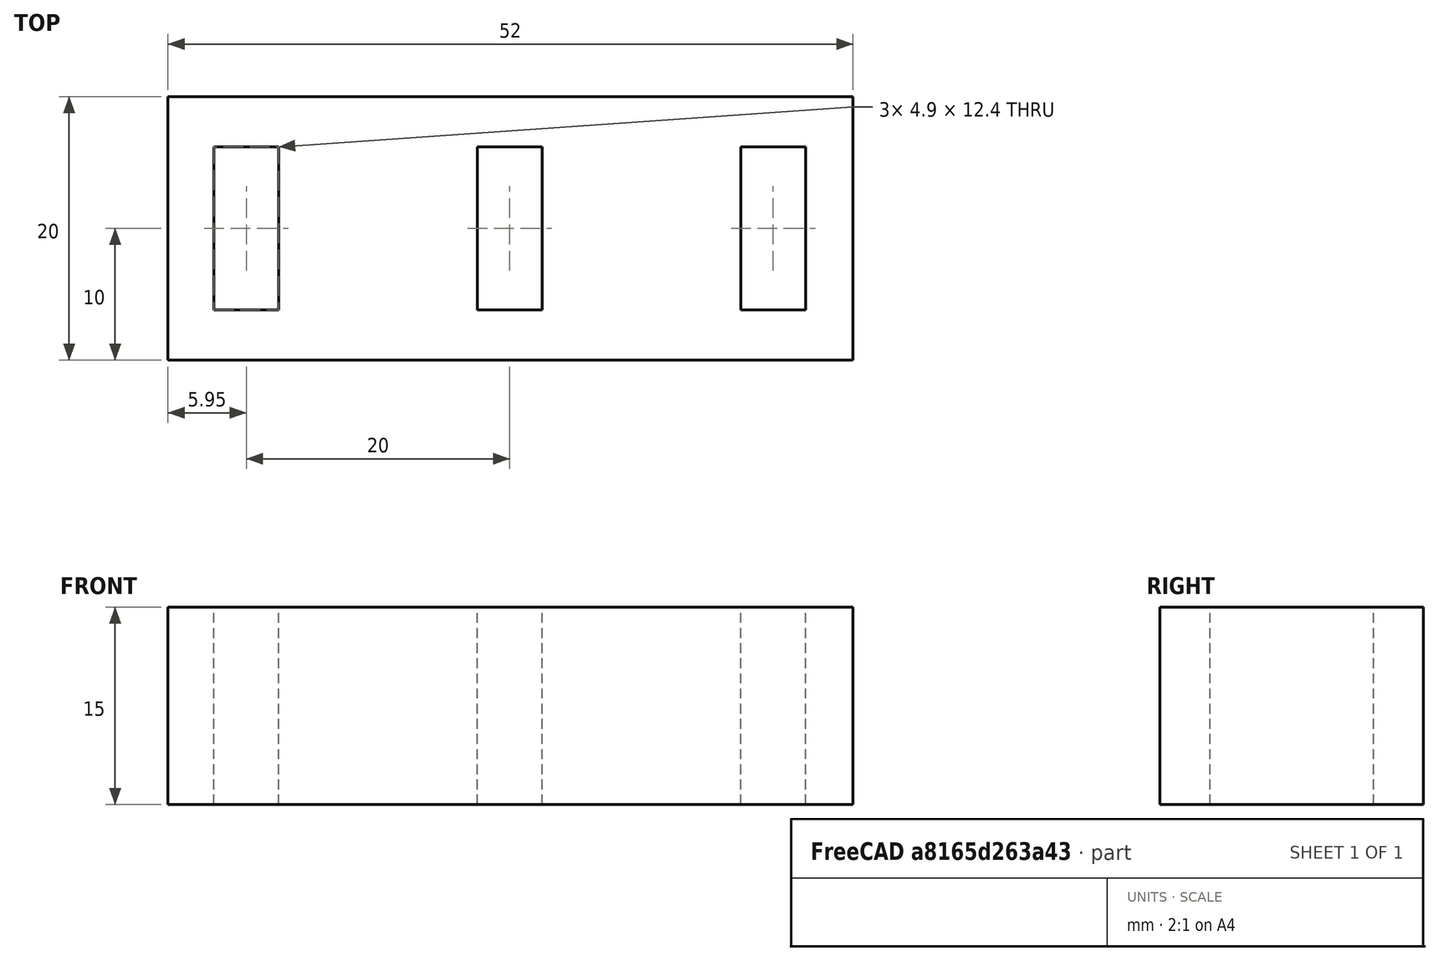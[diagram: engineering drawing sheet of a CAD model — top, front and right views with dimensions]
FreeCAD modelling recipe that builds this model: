
FCSTD DOCUMENT  (FreeCAD 1.0R38806 (Git))
Label: portapendrives
License: All rights reserved
LicenseURL: https://en.wikipedia.org/wiki/All_rights_reserved
objects: App::FeaturePython×8, Part::Box×4, Part::MultiFuse×1, Part::Cut×1
note: 6 computed .brp shape members not serialized (recipe doc carries the construction recipe); baked Part::Feature solids carry a one-line shape summary decoded from their .brp

FEATURE [Part::Box] Box  label="Cube"
  AttacherType = Attacher::AttachEngine3D
  Height = 15
  Length = 52
  Width = 20
FEATURE [Part::Box] Box001  label="Cube001"
  AttacherType = Attacher::AttachEngine3D
  Height = 23
  Length = 4.9
  Placement = pos=(3.5,3.8,-3) rot=(0,0,1;0rad)
  Width = 12.4
FEATURE [Part::Box] Box002  label="Cube002"
  AttacherType = Attacher::AttachEngine3D
  Height = 23
  Length = 4.9
  Placement = pos=(23.5,3.8,-3) rot=(0,0,1;0rad)
  Width = 12.4
FEATURE [Part::Box] Box003  label="Cube003"
  AttacherType = Attacher::AttachEngine3D
  Height = 23
  Length = 4.9
  Placement = pos=(43.5,3.8,-3) rot=(0,0,1;0rad)
  Width = 12.4
FEATURE [Part::MultiFuse] Fusion
  Refine = true
  Shapes = -> [Box003,Box002,Box001]
FEATURE [Part::Cut] Cut
  Base = -> Box
  Refine = true
  Tool = -> Fusion
FEATURE [App::FeaturePython] Dimension  # Draft dimension (typed FeaturePython)
  Diameter = false
  Dimline = (0,16.2,15)
  Direction = (0,0,0)
  Distance = 3.5
  End = (0,16.2,15)
  Normal = (0,0,1)
  Start = (3.5,16.2,15)
FEATURE [App::FeaturePython] Dimension001  # Draft dimension (typed FeaturePython)
  Diameter = false
  Dimline = (52,20.4279,15)
  Direction = (0,0,0)
  Distance = 52
  End = (52,20,15)
  Normal = (0,0,1)
  Start = (0,20,15)
FEATURE [App::FeaturePython] Dimension002  # Draft dimension (typed FeaturePython)
  Diameter = false
  Dimline = (8.4,3.8,15)
  Direction = (0,0,0)
  Distance = 12.4
  End = (8.4,3.8,15)
  Normal = (0,0,1)
  Start = (8.4,16.2,15)
FEATURE [App::FeaturePython] Dimension003  # Draft dimension (typed FeaturePython)
  Diameter = false
  Dimline = (28.4,3.8,15)
  Direction = (0,0,0)
  Distance = 4.9
  End = (28.4,3.8,15)
  Normal = (0,0,1)
  Start = (23.5,3.8,15)
FEATURE [App::FeaturePython] Dimension004  # Draft dimension (typed FeaturePython)
  Diameter = false
  Dimline = (48.4,16.2,15)
  Direction = (0,0,0)
  Distance = 20
  End = (48.4,16.2,15)
  Normal = (0,0,1)
  Start = (28.4,16.2,15)
FEATURE [App::FeaturePython] Dimension005  # Draft dimension (typed FeaturePython)
  Diameter = false
  Dimline = (48.4,16.2,15)
  Direction = (0,0,0)
  Distance = 20
  End = (48.4,16.2,15)
  Normal = (0,0,1)
  Start = (28.4,16.2,15)
FEATURE [App::FeaturePython] Dimension006  # Draft dimension (typed FeaturePython)
  Diameter = false
  Dimline = (52,20.5377,-0.911042)
  Direction = (0,0,0)
  Distance = 15
  End = (52,20,0)
  Normal = (1,0,0)
  Start = (52,20,15)
FEATURE [App::FeaturePython] Dimension007  # Draft dimension (typed FeaturePython)
  Diameter = false
  Dimline = (52,20,0)
  Direction = (0,0,0)
  Distance = 20
  End = (52,20,0)
  Normal = (1,0,0)
  Start = (52,0,0)
